# Revit family: Gira_511300
name_source: partatom
category: Allgemeines Modell
revit_build: Autodesk Revit 2017 (Build: 20160225_1515(x64)
units: mm (PartAtom-declared; Revit-internal decimal feet)

## family parameters
Basisbauteil = Fläche
Beim Laden mit Abzugskörper schneiden = Nein
Bemaßung runder Anschluss = Durchmesser verwenden
Gemeinsam genutzt = Nein
Kann Basisbauteil für Bewehrung sein = Nein
Raumberechnungspunkt = Nein
Teiletyp = Normal

## types (1)
- Gira_511300
    BIM = https://media.stage.bim.site
    Beschreibung = KNX PB sens.3 Basic 3g Sys55,KNX pushbutton sensor 3 Basis, 3-gang,System 55, Gira E22,Start-up rocker,Features:,- Mounting on bus coupler 3.,- Disassembly safeguard by screw connection.,- Rocker function: Switching, dimming, blind, value transmitter 1-byte, and scene auxiliary unit.,- White operating LED.,- Two red status LEDs per operating surface.,- Inscription space illumination for rocker sets with inscription space.,- Function of inscription space illumination and status LED can be configured.,,Notes :,- Professional labelling with the Gira Inscription Service www.marking.gira.com.,- The pushbutton sensor is supplied with a program-neutral start-up rocker. The suitable rocker set for the design line must be ordered separately.
    Bus connection included = Nein
    Bus system KNX = Ja
    Bus system KNX radio = Nein
    Bus system LON = Nein
    Bus system Powernet = Nein
    Bus system radio frequent = Nein
    Colour = Other
    Data sheet = https://katalog.gira.de
    Degree of protection (IP) = IP20
    GTIN = 4010337086826
    HAN = 511300
    Hersteller = Gira
    Material = Other
    Material quality = Other
    Mounting method = Flush mounted (plaster)
    Number of actuation points = 6
    Number of buttons = 3
    Other bus systems = None
    Productwebsite = http://katalog.gira.de
    Surface finishing = Not applicable
    Surface protection = Other
    Transparent = Nein
    Typname = KNX PB sens.3 Basis 3-g System 55, Gira E22
    URL = https://www.gira.de
    Vorgabe-Ansicht = 1219 mm
    With IR sensor = Nein
    With LED indication = Ja
    With anti-theft/dismantling protection = Ja
    With display = Nein
    With label area = Nein
    With room temperature controller = Nein

## geometry (parser evidence)
native form markers: Sweep x2
no freeform markers — native parametric forms only
